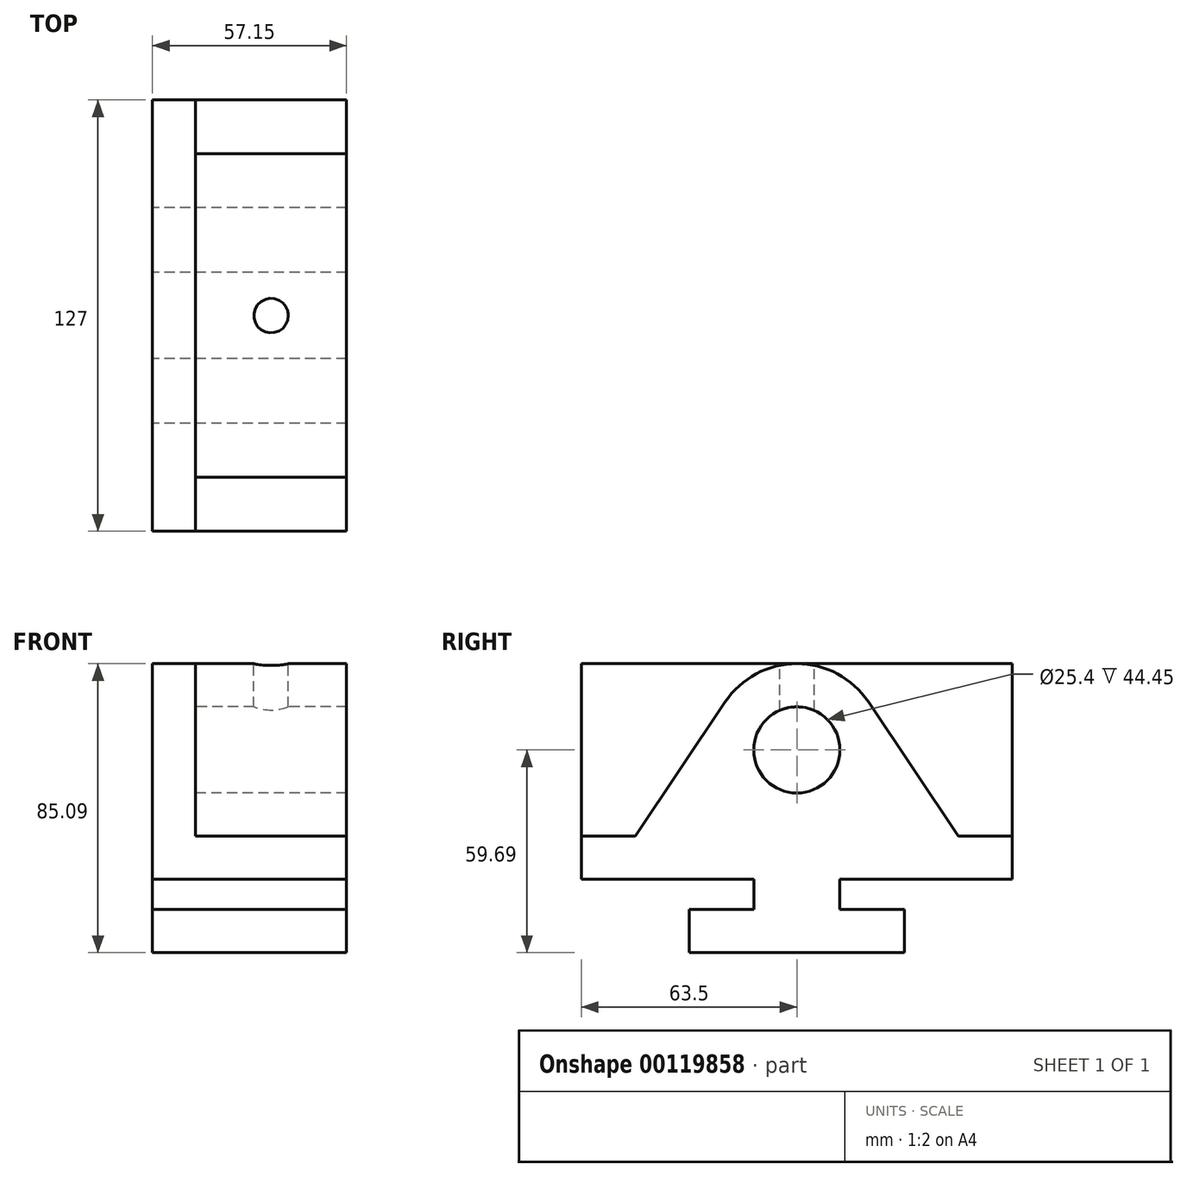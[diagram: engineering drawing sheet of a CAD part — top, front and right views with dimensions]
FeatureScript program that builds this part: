
annotation { "Feature Type Name" : "Feature", "Feature Type Description" : "" }
export const myFeature = defineFeature(function(context is Context, id is Id, definition is map)
    precondition{}
    {
        {
            var Q0;
            Q0=qCreatedBy(makeId("Right.planeOp"),FACE);
            var sketch = newSketch(context, id + "F0", { "sketchPlane" : qUnion([Q0])});
            skLineSegment(sketch, "E0", {"start": v(0, 0) * mm, "end": v(-31.75, 0) * mm});
            skLineSegment(sketch, "E1", {"start": v(-31.75, 0) * mm, "end": v(-31.75, 12.7) * mm});
            skLineSegment(sketch, "E2", {"start": v(-31.75, 12.7) * mm, "end": v(-12.7, 12.7) * mm});
            skLineSegment(sketch, "E3", {"start": v(-12.7, 12.7) * mm, "end": v(-12.7, 21.59) * mm});
            skLineSegment(sketch, "E4", {"start": v(-12.7, 21.59) * mm, "end": v(-63.5, 21.59) * mm});
            skLineSegment(sketch, "E5", {"start": v(-63.5, 21.6) * mm, "end": v(-63.5, 85.1) * mm});
            skLineSegment(sketch, "E6", {"start": v(0, 0) * mm, "end": v(0, 85.09) * mm, "construction": true});
            skLineSegment(sketch, "E7", {"start": v(0, 85.1) * mm, "end": v(-63.5, 85.1) * mm});
            skLineSegment(sketch, "E8.MirrorCS", {"start": v(31.75, 0) * mm, "end": v(31.75, 12.7) * mm});
            skLineSegment(sketch, "E9.MirrorCS", {"start": v(12.7, 21.59) * mm, "end": v(63.5, 21.59) * mm});
            skLineSegment(sketch, "E10.MirrorCS", {"start": v(63.5, 21.6) * mm, "end": v(63.5, 85.1) * mm});
            skLineSegment(sketch, "E11.MirrorCS", {"start": v(31.75, 12.7) * mm, "end": v(12.7, 12.7) * mm});
            skLineSegment(sketch, "E12.MirrorCS", {"start": v(12.7, 12.7) * mm, "end": v(12.7, 21.59) * mm});
            skLineSegment(sketch, "E13", {"start": v(0, 85.1) * mm, "end": v(63.5, 85.1) * mm});
            skLineSegment(sketch, "E14", {"start": v(31.75, 0) * mm, "end": v(0, 0) * mm});
            skLineSegment(sketch, "E15", {"start": v(63.5, 34.3) * mm, "end": v(47.62, 34.3) * mm});
            skLineSegment(sketch, "E16", {"start": v(-63.5, 34.3) * mm, "end": v(-47.63, 34.3) * mm});
            skLineSegment(sketch, "E17", {"start": v(-47.63, 34.29) * mm, "end": v(-21.1, 73.84) * mm});
            skLineSegment(sketch, "E18", {"start": v(47.63, 34.29) * mm, "end": v(21.1, 73.84) * mm});
            skArc(sketch, "E19", {"start": v(21.1, 73.84) * mm, "mid": v(0, 85.09) * mm, "end": v(-21.1, 73.84) * mm});
            skCircle(sketch, "E20", {"center": v(0, 59.69) * mm, "radius": 12.7 * mm});
            skSolve(sketch);
        }
        {
            var Q0;
            Q0=makeQuery(id+"F0.imprint","IMPRINT",FACE,{"disambiguationData":[TD([[makeQuery(id+"F0.imprint","IMPRINT",EDGE,{"derivedFrom":sQuery(id+"F0.wireOp",EDGE,"E0")}),-1.0]])]});
            extrude(context, id + "F1", {"entities" : qUnion([Q0]), "depth" : 44.45 * mm});
        }
        {
            var Q0;
            Q0=makeQuery(id+"F1.opExtrude","CAP_FACE",FACE,{"disambiguationData":[OSD([sQuery(id+"F0.wireOp",EDGE,"E0"),sQuery(id+"F0.wireOp",EDGE,"E1"),sQuery(id+"F0.wireOp",EDGE,"E2"),sQuery(id+"F0.wireOp",EDGE,"E3"),sQuery(id+"F0.wireOp",EDGE,"E4"),sQuery(id+"F0.wireOp",EDGE,"E5"),sQuery(id+"F0.wireOp",EDGE,"E8.MirrorCS"),sQuery(id+"F0.wireOp",EDGE,"E9.MirrorCS"),sQuery(id+"F0.wireOp",EDGE,"E10.MirrorCS"),sQuery(id+"F0.wireOp",EDGE,"E11.MirrorCS"),sQuery(id+"F0.wireOp",EDGE,"E12.MirrorCS"),sQuery(id+"F0.wireOp",EDGE,"E14"),sQuery(id+"F0.wireOp",EDGE,"E15"),sQuery(id+"F0.wireOp",EDGE,"E16"),sQuery(id+"F0.wireOp",EDGE,"E17"),sQuery(id+"F0.wireOp",EDGE,"E18"),sQuery(id+"F0.wireOp",EDGE,"E19"),sQuery(id+"F0.wireOp",EDGE,"E20")])],"isStart":true});
            var sketch = newSketch(context, id + "F2", { "sketchPlane" : qUnion([Q0])});
            skLineSegment(sketch, "E21.bottom", {"start": v(-63.5, 34.3) * mm, "end": v(63.5, 34.3) * mm});
            skLineSegment(sketch, "E21.top", {"start": v(-63.5, 21.6) * mm, "end": v(63.5, 21.6) * mm});
            skLineSegment(sketch, "E21.left", {"start": v(-63.5, 34.3) * mm, "end": v(-63.5, 21.6) * mm});
            skLineSegment(sketch, "E21.right", {"start": v(63.5, 34.3) * mm, "end": v(63.5, 21.6) * mm});
            skSolve(sketch);
        }
        {
            var Q0;
            {var subQ1=sQuery(id+"F0.wireOp",EDGE,"E7");Q0=makeQuery(id+"F0.imprint","IMPRINT",FACE,{"disambiguationData":[TD([[makeQuery(id+"F0.imprint","IMPRINT",EDGE,{"derivedFrom":subQ1}),1.0]])]});}
            var Q1;
            {var subQ2=sQuery(id+"F0.wireOp",EDGE,"E13");Q1=makeQuery(id+"F0.imprint","IMPRINT",FACE,{"disambiguationData":[TD([[makeQuery(id+"F0.imprint","IMPRINT",EDGE,{"derivedFrom":subQ2}),-1.0]])]});}
            var Q2;
            {var subQ5=sQuery(id+"F2.wireOp",EDGE,"E21.left");Q2=makeQuery(id+"F2.imprint","IMPRINT",FACE,{"disambiguationData":[TD([[makeQuery(id+"F2.imprint","IMPRINT",EDGE,{"derivedFrom":subQ5}),-1.0]])]});}
            var Q3;
            Q3=makeQuery(id+"F0.imprint","IMPRINT",FACE,{"disambiguationData":[TD([[makeQuery(id+"F0.imprint","IMPRINT",EDGE,{"derivedFrom":sQuery(id+"F0.wireOp",EDGE,"E20")}),1.0]])]});
            var Q4;
            Q4=makeQuery(id+"F0.imprint","IMPRINT",FACE,{"disambiguationData":[TD([[makeQuery(id+"F0.imprint","IMPRINT",EDGE,{"derivedFrom":sQuery(id+"F0.wireOp",EDGE,"E0")}),-1.0]])]});
            extrude(context, id + "F3", {"entities" : qUnion([Q0, Q1, Q2, Q3, Q4]), "operationType" : NewBodyOperationType.ADD, "oppositeDirection" : true, "depth" : 12.7 * mm});
        }
        {
            var Q0;
            Q0=makeQuery(id+"F3.opExtrude","SWEPT_FACE",FACE,{"disambiguationData":[OSD([sQuery(id+"F0.wireOp",EDGE,"E7"),sQuery(id+"F0.wireOp",EDGE,"E13")])]});
            var sketch = newSketch(context, id + "F4", { "sketchPlane" : qUnion([Q0])});
            skLineSegment(sketch, "E22", {"start": v(0, 0) * mm, "end": v(43.32, 0) * mm, "construction": true});
            skLineSegment(sketch, "E23", {"start": v(22.23, 0) * mm, "end": v(22.22, 42.6) * mm, "construction": true});
            skCircle(sketch, "E24", {"center": v(22.23, 0) * mm, "radius": 5.08 * mm});
            skSolve(sketch);
        }
        {
            var Q0;
            Q0 = qSketchRegion(id + "F4", true);
            extrude(context, id + "F5", {"entities" : qUnion([Q0]), "operationType" : NewBodyOperationType.REMOVE, "endBound" : BoundingType.UP_TO_NEXT, "oppositeDirection" : true, "depth" : 25.4 * mm});
        }
    });
